# Revit family: Dämmelement DHL
name_source: partatom
category: HLS-Bauteile
revit_build: Autodesk Revit 2017 (Build: 20190507_1515(x64)
units: mm (PartAtom-declared; Revit-internal decimal feet)

## family parameters
Arbeitsebenenbasiert = Nein
Beim Laden mit Abzugskörper schneiden = Nein
Bemaßung runder Anschluss = Durchmesser verwenden
Gemeinsam genutzt = Ja
Immer vertikal = Ja
Raumberechnungspunkt = Nein
Teiletyp = Normal

## types (2) — shared parameters
DF1 = 40 mm  [stored 0.131234 ft]
DF2 = 27 mm  [stored 0.0885827 ft]
Fabrikat = MEFA
Firma = MEFA Befestigungs- und Montagesysteme GmbH
Kurztext1 = Dämmelement DHL
MB = 30 mm  [stored 0.0984252 ft]
Material = Stahl
Materialname = S235
Mengeneinheit = St
Oberflaeche = galvanisch verzinkt
Schalldämmeinlage = Gummi SBR
d2 = 31 mm  [stored 0.101706 ft]
d3 = 44 mm  [stored 0.144357 ft]
max. Temperaturbeständigkeit = 100 °C
max. zul. Last = 1.00 kN
max. zul. Last Druck = 0.00 kN
vpe = 50 St

## per-type parameters (varying)
| type | Artikelnummer | EAN | Gewicht | Gewicht pro Bauteil | Gewinde | Kurztext2 | d1 |
| DHL Dämmelent M 8 | 0783301 | 4250928418753 | 0.09 kg | 0.09 kg | M8 | M8 | 8 mm  [stored 0.0262467 ft] |
| DHL Dämmelent M10 | 0783302 | 4250928418760 | 0.10 kg | 0.10 kg | M10 | M10 | 10 mm  [stored 0.0328084 ft] |

note: [stored X ft] marks values corroborated as IEEE doubles in the binary element streams (Revit-internal decimal feet)
